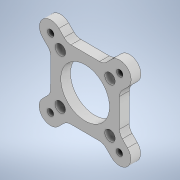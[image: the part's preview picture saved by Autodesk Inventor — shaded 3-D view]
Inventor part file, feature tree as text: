
AUTODESK INVENTOR PART (.ipt)
format: ipt  version: 2020 (Build 240168000, 168)  size: 296,960 bytes
history: native  units: mm
features: extrude x4, sketch x4, other x4, projected_geometry x3, fillet x1, reference x1
ambient origin geometry x8: Origin, YZ Plane, XZ Plane, XY Plane, X Axis, Y Axis, Z Axis, Center Point
bodies: Solid1 (feature_tree)
feature tree (17):
  extrude  "Extrusion1"  Depth=3.0mm
  extrude  "Extrusion2"  Depth=3.0mm
  extrude  "Extrusion3"  Depth=15.0mm
  fillet  "Fillet2"  Radius=2.0mm
  extrude  "Extrusion4"  Depth=3.0mm TaperAngle=360.0deg
  sketch  "Sketch1"  dims[d0=3.0mm d1=3.0mm]
  reference  "Reference1"
  sketch  "Sketch2"  dims[d2=3.0mm d3=3.0mm]
  projected_geometry  "Projected Loop1"
  sketch  "Sketch3"  dims[d5=15.0mm d6=5.0mm d7=2.0mm]
  projected_geometry  "Projected Loop2"
  sketch  "Sketch4"  dims[d8=15.0mm d9=40.0mm d11=360.0deg d13=7.0mm d14=7.0mm d15=7.0mm d16=7.0mm d17=24.0mm d18=3.0mm d19=0.0mm d20=15.0mm d21=3.0mm d22=0.0mm d24=3.0mm d25=0.0mm d26=3.0mm d27=3.2mm d28=3.2mm d29=3.2mm d30=3.2mm d31=3.0mm d32=0.0mm]
  projected_geometry  "Projected Loop3"
  parser-record x1  (decoder bookkeeping rows leaked as tree rows — omitted from the tree; the rows remain in map.json)
  other  "encoder_arr_1.iam"
  other  "encoder_as5047p:1"
  other  "Board:1"
note: 1 file-system path scrubbed to <path> (originals preserved in map.json)
